# Revit family: Турникет тумбовый PERCo_TTD-03.2
name_source: partatom
category: Оборудование
units: mm (PartAtom-declared; Revit-internal decimal feet)

## family parameters
Всегда вертикально = Нет
Классификация = Нет
На основе рабочей плоскости = Нет
Общий = Нет
При загрузке вырезать с полостями = Нет
Размер круглого соединителя = Использовать диаметр
Тип детали = Нормальный
Точка расчета площади = Нет

## types (2) — shared parameters
ADSK_URL страницы изделия = https://www.perco.ru
ADSK_Единица измерения = шт.
ADSK_Завод-изготовитель = PERCo
ADSK_Количество = 1
ADSK_Масса_Текст = не более 60 кг
ADSK_Напряжение = 12 В
ADSK_Номинальная мощность = 9 Вт
ADSK_Ток = 1 А
Встраивание считывателей внутрь = Нет
Габаритные размеры (длина×ширина×высота) = 980 х 664 x 1010 мм
Габаритные размеры контроллера для встраивания в нишу = не более 250 ×175 ×40 мм
Габаритные размеры считывателя для встраивания в ниши = не более 100×130×28 мм
Длина планки = 511 мм
Емкость картоприёмника = Не предусмотренно
Крышка = Нержавейка
Подключение к электросети = 220 В
Пропускная способность = 30 чел./мин
Степень защиты оболочки = IP41
Температура использования = от +1°С до +50°С
Ширина зоны прохода = 500 мм.

## per-type parameters (varying)
| type | ADSK_Материал наименование | ADSK_Наименование | ADSK_Наименование краткое | Корпус |
| TTD-03.2G | Крышка выполнена из нержавеющей стали, корпус - из стали, окрашенной порошковой краской | Турникет тумбовый PERCo-TTD-03.2G для эксплуатации в закрытых помещениях | Турникет тумбовый TTD-03.2G | Сталь окрашенная порошковой краской |
| TTD-03.2S | Корпус, верхняя крышка, планки выполнены из нержавеющей стали | Турникет тумбовый PERCo-TTD-03.2S для эксплуатации в закрытых помещениях | Турникет тумбовый TTD-03.2S | Нержавейка |
